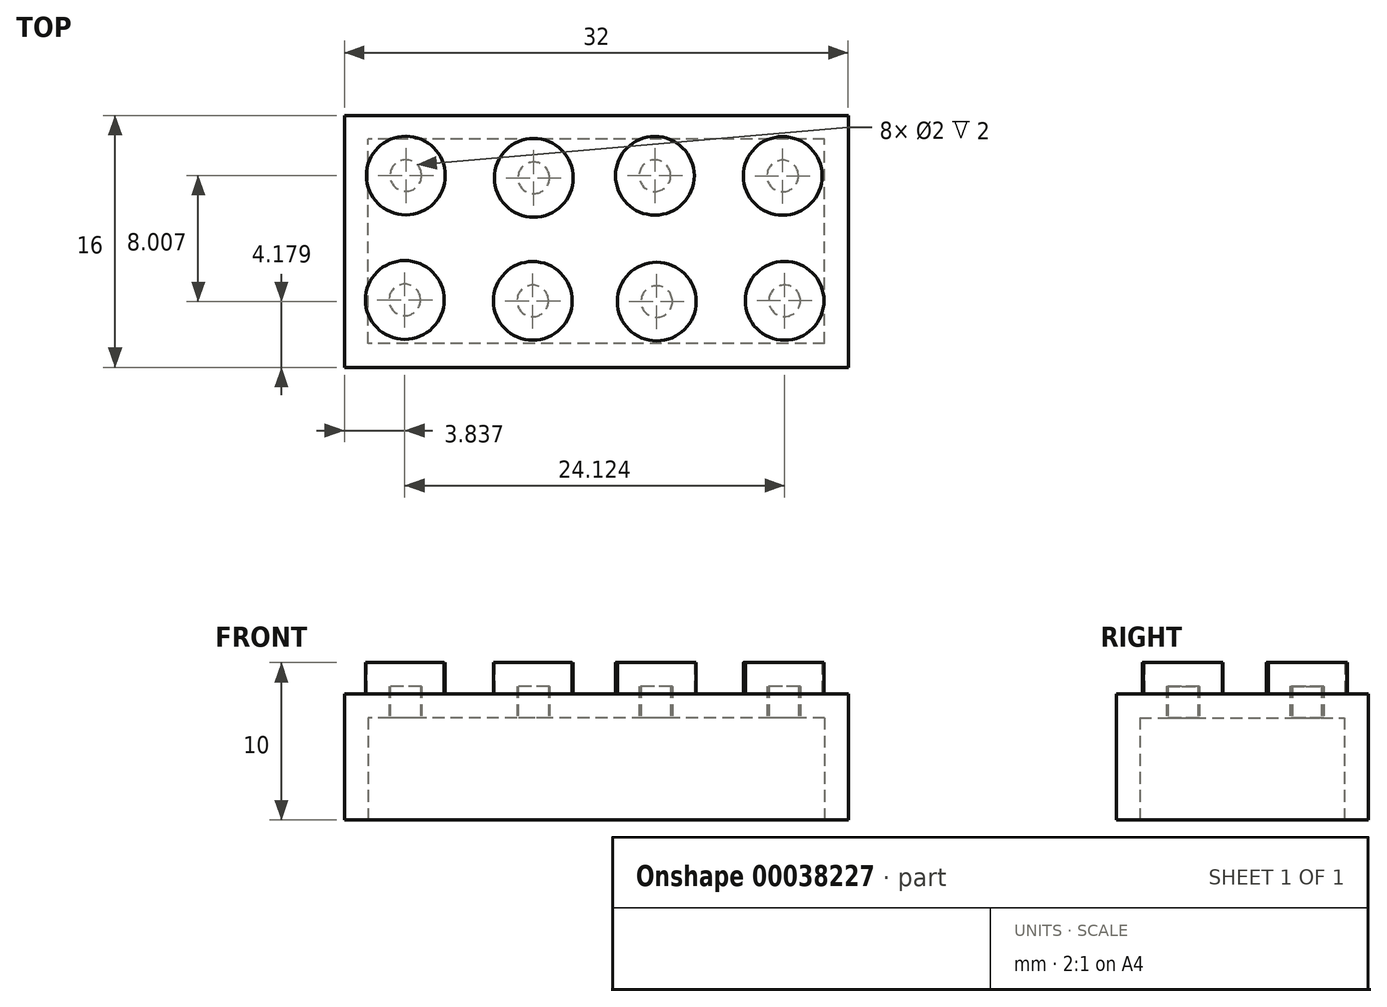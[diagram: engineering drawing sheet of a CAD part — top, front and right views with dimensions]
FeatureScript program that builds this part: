
annotation { "Feature Type Name" : "Feature", "Feature Type Description" : "" }
export const myFeature = defineFeature(function(context is Context, id is Id, definition is map)
    precondition{}
    {
        {
            var Q0;
            Q0=qCreatedBy(makeId("Top.planeOp"),FACE);
            var sketch = newSketch(context, id + "F0", { "sketchPlane" : qUnion([Q0])});
            skLineSegment(sketch, "E0.rect.bottom", {"start": v(-13.67, 9.64) * mm, "end": v(-45.67, 9.64) * mm});
            skLineSegment(sketch, "E0.rect.top", {"start": v(-13.67, 25.64) * mm, "end": v(-45.67, 25.64) * mm});
            skLineSegment(sketch, "E0.rect.left", {"start": v(-13.67, 9.64) * mm, "end": v(-13.67, 25.64) * mm});
            skLineSegment(sketch, "E0.rect.right", {"start": v(-45.67, 9.64) * mm, "end": v(-45.67, 25.64) * mm});
            skPoint(sketch, "E0.rect.middle", {"position": v(-29.67, 17.64) * mm});
            skLineSegment(sketch, "E1", {"start": v(-45.67, 25.64) * mm, "end": v(-45.67, 29.27) * mm, "construction": true});
            skLineSegment(sketch, "E2", {"start": v(-45.67, 29.27) * mm, "end": v(-13.61, 29.27) * mm, "construction": true});
            skLineSegment(sketch, "E3", {"start": v(-13.61, 29.27) * mm, "end": v(-13.67, 25.64) * mm, "construction": true});
            skLineSegment(sketch, "E4", {"start": v(-13.67, 25.64) * mm, "end": v(-9, 25.58) * mm, "construction": true});
            skLineSegment(sketch, "E5", {"start": v(-9, 25.01) * mm, "end": v(-9, 9.58) * mm, "construction": true});
            skLineSegment(sketch, "E6", {"start": v(-13.67, 9.64) * mm, "end": v(-9, 9.58) * mm, "construction": true});
            skLineSegment(sketch, "E7", {"start": v(-4, 0) * mm, "end": v(4, 0) * mm});
            skCircle(sketch, "E8", {"center": v(12.07, -3.95) * mm, "radius": 2.5 * mm});
            skCircle(sketch, "E9", {"center": v(-3.92, -3.96) * mm, "radius": 2.5 * mm});
            skCircle(sketch, "E10", {"center": v(-3.86, 3.85) * mm, "radius": 2.5 * mm});
            skCircle(sketch, "E11", {"center": v(3.95, -4) * mm, "radius": 2.5 * mm});
            skCircle(sketch, "E12", {"center": v(3.84, 3.99) * mm, "radius": 2.5 * mm});
            skCircle(sketch, "E13", {"center": v(11.95, 3.98) * mm, "radius": 2.5 * mm});
            skCircle(sketch, "E14", {"center": v(-11.98, 4) * mm, "radius": 2.5 * mm});
            skCircle(sketch, "E15", {"center": v(-12.05, -3.9) * mm, "radius": 2.5 * mm});
            skSolve(sketch);
        }
        {
            var Q0;
            Q0=makeQuery(id+"F0.imprint","IMPRINT",FACE,{"disambiguationData":[TD([[makeQuery(id+"F0.imprint","IMPRINT",EDGE,{"derivedFrom":sQuery(id+"F0.wireOp",EDGE,"E0.rect.bottom")}),-1.0]])]});
            extrude(context, id + "F1", {"entities" : qUnion([Q0]), "depth" : 8 * mm});
        }
        {
            var Q0;
            Q0=qCreatedBy(makeId("Top.planeOp"),FACE);
            cPlane(context, id + "F2", {"entities" : qUnion([Q0]), "cplaneType" : CPlaneType.OFFSET, "offset" : 8 * mm, "width" : 150 * mm, "height" : 150 * mm});
        }
        {
            var Q0;
            Q0=qCreatedBy(id+"F2.planeOp",FACE);
            var sketch = newSketch(context, id + "F3", { "sketchPlane" : qUnion([Q0])});
            skCircle(sketch, "E16", {"center": v(-41.77, 21.83) * mm, "radius": 2.5 * mm});
            skCircle(sketch, "E17", {"center": v(-33.64, 21.68) * mm, "radius": 2.5 * mm});
            skCircle(sketch, "E18", {"center": v(-25.95, 21.81) * mm, "radius": 2.5 * mm});
            skCircle(sketch, "E19", {"center": v(-17.83, 21.8) * mm, "radius": 2.5 * mm});
            skCircle(sketch, "E20", {"center": v(-41.83, 13.93) * mm, "radius": 2.5 * mm});
            skCircle(sketch, "E21", {"center": v(-33.7, 13.86) * mm, "radius": 2.5 * mm});
            skCircle(sketch, "E22", {"center": v(-25.83, 13.82) * mm, "radius": 2.5 * mm});
            skCircle(sketch, "E23", {"center": v(-17.7, 13.87) * mm, "radius": 2.5 * mm});
            skSolve(sketch);
        }
        {
            var Q0;
            Q0=makeQuery(id+"F3.imprint","IMPRINT",FACE,{"disambiguationData":[TD([[makeQuery(id+"F3.imprint","IMPRINT",EDGE,{"derivedFrom":sQuery(id+"F3.wireOp",EDGE,"E19")}),1.0]])]});
            var Q1;
            Q1=makeQuery(id+"F3.imprint","IMPRINT",FACE,{"disambiguationData":[TD([[makeQuery(id+"F3.imprint","IMPRINT",EDGE,{"derivedFrom":sQuery(id+"F3.wireOp",EDGE,"E18")}),1.0]])]});
            var Q2;
            Q2=makeQuery(id+"F3.imprint","IMPRINT",FACE,{"disambiguationData":[TD([[makeQuery(id+"F3.imprint","IMPRINT",EDGE,{"derivedFrom":sQuery(id+"F3.wireOp",EDGE,"E17")}),1.0]])]});
            var Q3;
            Q3=makeQuery(id+"F3.imprint","IMPRINT",FACE,{"disambiguationData":[TD([[makeQuery(id+"F3.imprint","IMPRINT",EDGE,{"derivedFrom":sQuery(id+"F3.wireOp",EDGE,"E22")}),1.0]])]});
            var Q4;
            Q4=makeQuery(id+"F3.imprint","IMPRINT",FACE,{"disambiguationData":[TD([[makeQuery(id+"F3.imprint","IMPRINT",EDGE,{"derivedFrom":sQuery(id+"F3.wireOp",EDGE,"E21")}),1.0]])]});
            var Q5;
            Q5=makeQuery(id+"F3.imprint","IMPRINT",FACE,{"disambiguationData":[TD([[makeQuery(id+"F3.imprint","IMPRINT",EDGE,{"derivedFrom":sQuery(id+"F3.wireOp",EDGE,"E23")}),1.0]])]});
            var Q6;
            Q6=makeQuery(id+"F3.imprint","IMPRINT",FACE,{"disambiguationData":[TD([[makeQuery(id+"F3.imprint","IMPRINT",EDGE,{"derivedFrom":sQuery(id+"F3.wireOp",EDGE,"E20")}),1.0]])]});
            var Q7;
            Q7=makeQuery(id+"F3.imprint","IMPRINT",FACE,{"disambiguationData":[TD([[makeQuery(id+"F3.imprint","IMPRINT",EDGE,{"derivedFrom":sQuery(id+"F3.wireOp",EDGE,"E16")}),1.0]])]});
            extrude(context, id + "F4", {"entities" : qUnion([Q0, Q1, Q2, Q3, Q4, Q5, Q6, Q7]), "operationType" : NewBodyOperationType.ADD, "depth" : 2 * mm});
        }
        {
            var Q0;
            Q0=makeQuery(id+"F1.opExtrude","CAP_FACE",FACE,{"disambiguationData":[OSD([sQuery(id+"F0.wireOp",EDGE,"E0.rect.bottom"),sQuery(id+"F0.wireOp",EDGE,"E0.rect.top"),sQuery(id+"F0.wireOp",EDGE,"E0.rect.left"),sQuery(id+"F0.wireOp",EDGE,"E0.rect.right")])],"isStart":true});
            shell(context, id + "F5", {"entities" : qUnion([Q0]), "thickness" : 1.5 * mm});
        }
    });
